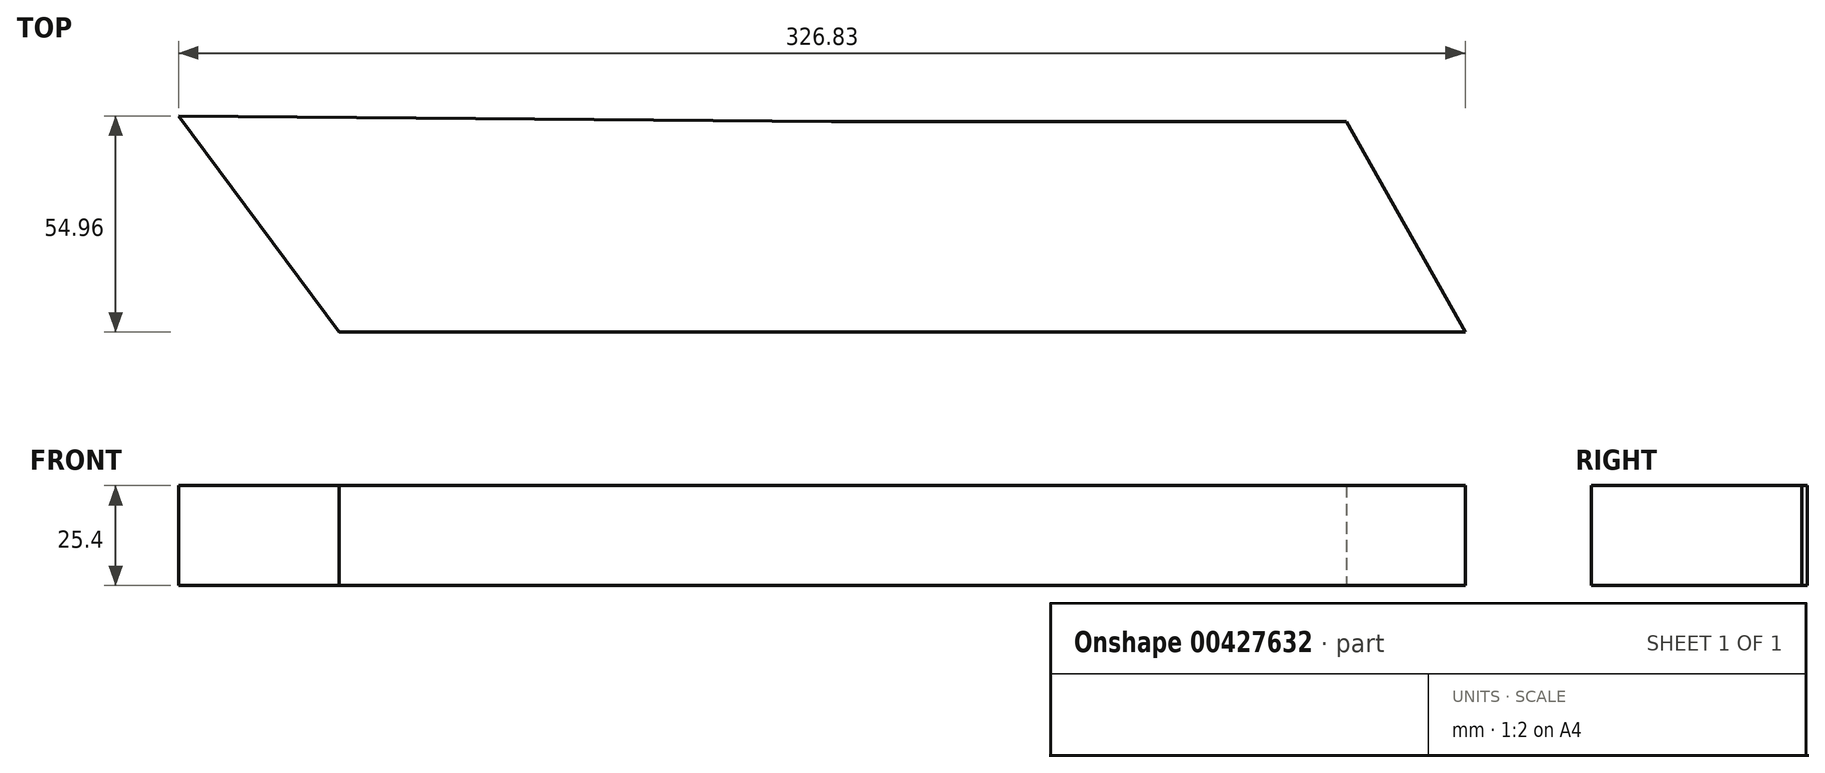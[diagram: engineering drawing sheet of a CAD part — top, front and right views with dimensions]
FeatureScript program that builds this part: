
annotation { "Feature Type Name" : "Feature", "Feature Type Description" : "" }
export const myFeature = defineFeature(function(context is Context, id is Id, definition is map)
    precondition{}
    {
        {
            var Q0;
            Q0=qCreatedBy(makeId("Top.planeOp"),FACE);
            var sketch = newSketch(context, id + "F0", { "sketchPlane" : qUnion([Q0])});
            skLineSegment(sketch, "E0", {"start": v(-125.08, -54.96) * mm, "end": v(-165.88, 0) * mm});
            skLineSegment(sketch, "E1", {"start": v(-165.88, 0) * mm, "end": v(0, -1.44) * mm});
            skLineSegment(sketch, "E2", {"start": v(0, -1.44) * mm, "end": v(130.84, -1.44) * mm});
            skLineSegment(sketch, "E3", {"start": v(130.84, -1.44) * mm, "end": v(160.95, -54.96) * mm});
            skLineSegment(sketch, "E4", {"start": v(160.95, -54.96) * mm, "end": v(-125.08, -54.96) * mm});
            skSolve(sketch);
        }
        {
            var Q0;
            Q0=makeQuery(id+"F0.imprint","IMPRINT",FACE,{"disambiguationData":[TD([[makeQuery(id+"F0.imprint","IMPRINT",EDGE,{"derivedFrom":sQuery(id+"F0.wireOp",EDGE,"E0")}),-1.0]])]});
            extrude(context, id + "F1", {"entities" : qUnion([Q0]), "depth" : 25.4 * mm});
        }
    });
